# Revit family: NLRS_63_LD_LUM-DL02AC-SNR_luminaid
name_source: partatom
category: Lighting Devices
revit_build: Autodesk Revit 2018 (Build: 20190510_1515(x64)
units: mm (PartAtom-declared; Revit-internal decimal feet)

## family parameters
Always vertical = Yes
Cut with Voids When Loaded = No
Maintain Annotation Orientation = Yes
Part Type = Switch
Room Calculation Point = No
Round Connector Dimension = Use Diameter
Shared = No
Work Plane-Based = No

## types (4) — shared parameters
Ambient temp range = -20 ±40°C
Angle = 180.00°
Depth = 130 mm  [stored 0.426509 ft]
Duration = 5 sec  - 15 mins
Height = 130 mm  [stored 0.426509 ft]
Housing = IP54
Housing material = Plastic
Input Voltage = 220-240, 50/60 Hz
Length = 180 mm  [stored 0.590551 ft]
Manufacturer = LUMINAID B.V.
Mounting height = 2-5m
Power = 1 W
Product Brand = DATALUX TRONIC
Sensor = PIR
Upside = No
Weight = 0.72 kg

## per-type parameters (varying)
| type | Sensor type |
| LUM-DL02AC-SNR-PRLC | Lowbay circular |
| LUM-DL02AC-SNR-PRLE | Lowbay elliptical |
| LUM-DL02AC-SNR-PRHC | Highbay circular |
| LUM-DL02AC-SNR-PRHE | Highbay elliptical |

note: column(s) folded — value = type name in every type: Article Code

note: [stored X ft] marks values corroborated as IEEE doubles in the binary element streams (Revit-internal decimal feet)

## geometry (parser evidence)
native form markers: Sweep x17
no freeform markers — native parametric forms only
